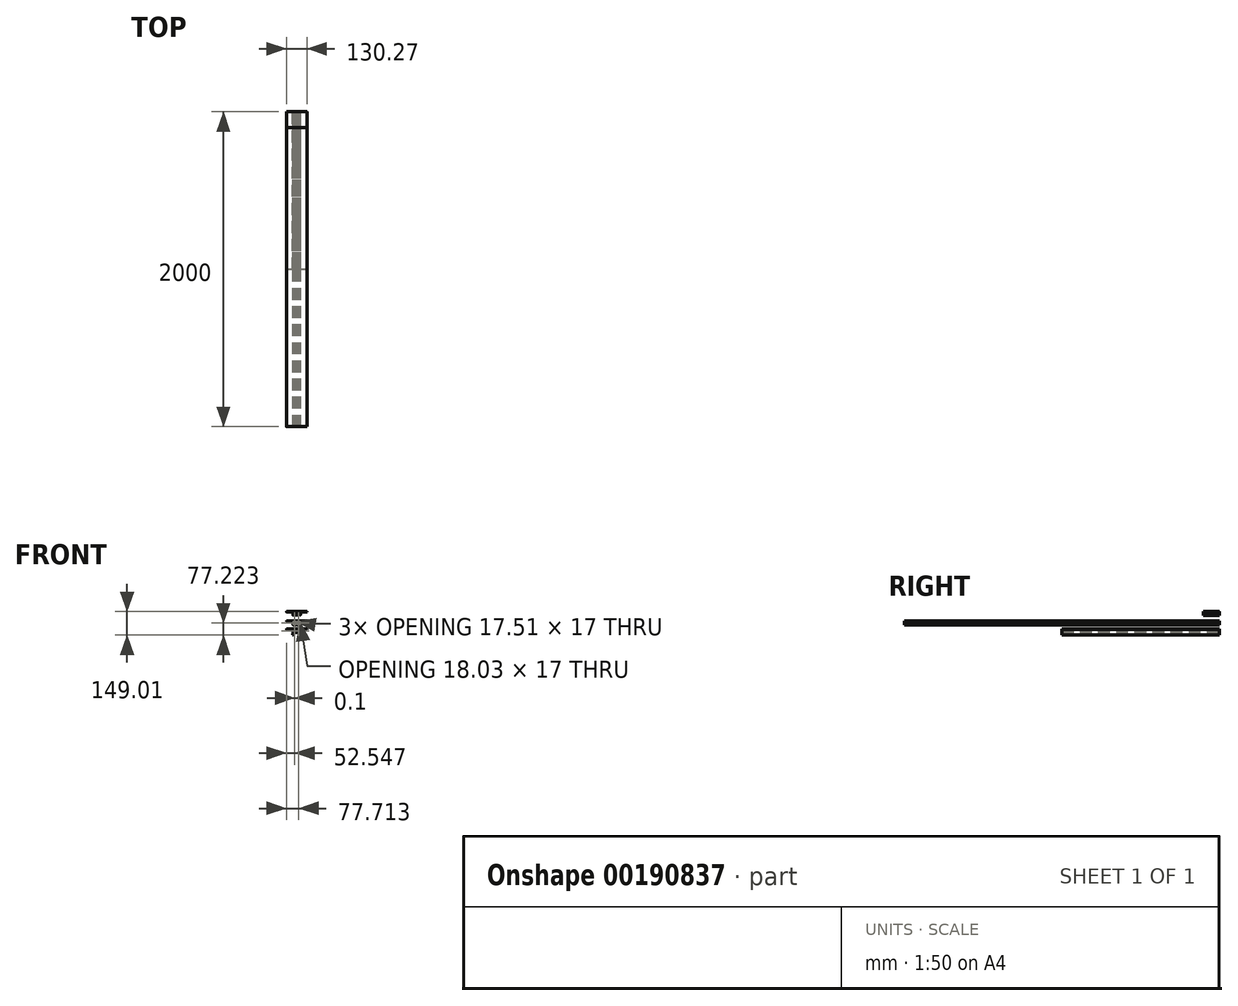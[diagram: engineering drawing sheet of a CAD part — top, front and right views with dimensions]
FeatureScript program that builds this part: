
annotation { "Feature Type Name" : "Feature", "Feature Type Description" : "" }
export const myFeature = defineFeature(function(context is Context, id is Id, definition is map)
    precondition{}
    {
        {
            var Q0;
            Q0=qCreatedBy(makeId("Front.planeOp"),FACE);
            var sketch = newSketch(context, id + "F0", { "sketchPlane" : qUnion([Q0])});
            skLineSegment(sketch, "E0", {"start": v(-63.5, 0) * mm, "end": v(63.5, 0) * mm});
            skLineSegment(sketch, "E1", {"start": v(-63.5, -3) * mm, "end": v(-25.2, -3) * mm});
            skLineSegment(sketch, "E2", {"start": v(24.22, -3) * mm, "end": v(63.5, -3) * mm});
            skLineSegment(sketch, "E3", {"start": v(-21.2, -7) * mm, "end": v(-21.2, -16) * mm});
            skLineSegment(sketch, "E4", {"start": v(-17.2, -20) * mm, "end": v(-10.5, -20) * mm});
            skLineSegment(sketch, "E5", {"start": v(-17.2, -3) * mm, "end": v(-5.7, -3) * mm});
            skArc(sketch, "E6", {"start": v(-4.66, -6.71) * mm, "mid": v(-8.45, -11.3) * mm, "end": v(-8.54, -17.26) * mm});
            skArc(sketch, "E7.filletArc", {"start": v(-4.66, -6.71) * mm, "mid": v(-3.77, -4.46) * mm, "end": v(-5.7, -3) * mm});
            skLineSegment(sketch, "E8", {"start": v(21.2, -7) * mm, "end": v(21.2, -7) * mm});
            skPoint(sketch, "E9.visualSharp", {"position": v(-21.2, -3) * mm});
            skArc(sketch, "E9.filletArc", {"start": v(-17.2, -3) * mm, "mid": v(-20.04, -4.17) * mm, "end": v(-21.2, -7) * mm});
            skPoint(sketch, "E10.visualSharp", {"position": v(-7.05, -20) * mm});
            skArc(sketch, "E10.filletArc", {"start": v(-10.5, -20) * mm, "mid": v(-8.82, -19.14) * mm, "end": v(-8.54, -17.26) * mm});
            skPoint(sketch, "E11.visualSharp", {"position": v(-21.2, -20) * mm});
            skArc(sketch, "E11.filletArc", {"start": v(-21.2, -16) * mm, "mid": v(-20.04, -18.83) * mm, "end": v(-17.2, -20) * mm});
            skPoint(sketch, "E12", {"position": v(-24.2, -23) * mm});
            skPoint(sketch, "E13", {"position": v(24.22, -23.12) * mm});
            skLineSegment(sketch, "E14", {"start": v(-24.2, -4) * mm, "end": v(-24.2, -22.88) * mm});
            skLineSegment(sketch, "E15", {"start": v(24.22, -3) * mm, "end": v(24.22, -23) * mm});
            skLineSegment(sketch, "E16.MirrorCS", {"start": v(25.48, -38) * mm, "end": v(25.48, -38) * mm});
            skArc(sketch, "E17", {"start": v(-63.5, 0) * mm, "mid": v(-65, -1.5) * mm, "end": v(-63.5, -3) * mm});
            skArc(sketch, "E18", {"start": v(63.5, -3) * mm, "mid": v(65, -1.5) * mm, "end": v(63.5, 0) * mm});
            skLineSegment(sketch, "E19", {"start": v(-24.22, -23.12) * mm, "end": v(-26.05, -38) * mm});
            skLineSegment(sketch, "E20", {"start": v(-24.3, -36.44) * mm, "end": v(-21.78, -24.58) * mm});
            skLineSegment(sketch, "E21", {"start": v(-19.82, -23) * mm, "end": v(-2.72, -23) * mm});
            skLineSegment(sketch, "E22", {"start": v(-1.72, -22) * mm, "end": v(-1.72, -20.86) * mm});
            skPoint(sketch, "E23.visualSharp", {"position": v(-21.44, -23) * mm});
            skArc(sketch, "E23.filletArc", {"start": v(-19.82, -23) * mm, "mid": v(-21.08, -23.45) * mm, "end": v(-21.78, -24.58) * mm});
            skPoint(sketch, "E24.visualSharp", {"position": v(-24.63, -38) * mm});
            skArc(sketch, "E24.filletArc", {"start": v(-26.05, -38) * mm, "mid": v(-24.92, -37.5) * mm, "end": v(-24.3, -36.44) * mm});
            skArc(sketch, "E25.filletArc", {"start": v(-24.22, -23.12) * mm, "mid": v(-24.21, -23) * mm, "end": v(-24.2, -22.88) * mm});
            skPoint(sketch, "E26.visualSharp", {"position": v(-24.2, -3) * mm});
            skArc(sketch, "E26.filletArc", {"start": v(-24.2, -4) * mm, "mid": v(-24.5, -3.3) * mm, "end": v(-25.2, -3) * mm});
            skPoint(sketch, "E27.visualSharp", {"position": v(-1.72, -23) * mm});
            skArc(sketch, "E28.filletArc", {"start": v(-1.72, -20.86) * mm, "mid": v(-1.89, -20.3) * mm, "end": v(-2.33, -19.94) * mm});
            skArc(sketch, "E29.MirrorCS", {"start": v(1.72, -20.86) * mm, "mid": v(1.89, -20.3) * mm, "end": v(2.33, -19.94) * mm});
            skLineSegment(sketch, "E30.MirrorCS", {"start": v(1.72, -22) * mm, "end": v(1.72, -20.86) * mm});
            skLineSegment(sketch, "E31.MirrorCS", {"start": v(19.82, -23) * mm, "end": v(2.72, -23) * mm});
            skArc(sketch, "E32.MirrorCS", {"start": v(19.82, -23) * mm, "mid": v(21.08, -23.45) * mm, "end": v(21.78, -24.58) * mm});
            skLineSegment(sketch, "E33.MirrorCS", {"start": v(24.3, -36.44) * mm, "end": v(21.78, -24.58) * mm});
            skLineSegment(sketch, "E34.MirrorCS", {"start": v(24.24, -23.24) * mm, "end": v(26.05, -38) * mm});
            skArc(sketch, "E35.MirrorCS", {"start": v(26.05, -38) * mm, "mid": v(24.92, -37.5) * mm, "end": v(24.3, -36.44) * mm});
            skArc(sketch, "E36", {"start": v(-2.33, -19.94) * mm, "mid": v(0, -8.41) * mm, "end": v(2.33, -19.94) * mm});
            skArc(sketch, "E37.filletArc", {"start": v(24.22, -23) * mm, "mid": v(24.23, -23.12) * mm, "end": v(24.24, -23.24) * mm});
            skArc(sketch, "E38.MirrorCS", {"start": v(4.66, -6.71) * mm, "mid": v(8.45, -11.3) * mm, "end": v(8.54, -17.26) * mm});
            skArc(sketch, "E39.MirrorCS", {"start": v(4.66, -6.71) * mm, "mid": v(3.77, -4.46) * mm, "end": v(5.7, -3) * mm});
            skArc(sketch, "E40.MirrorCS", {"start": v(17.2, -3) * mm, "mid": v(20.04, -4.17) * mm, "end": v(21.2, -7) * mm});
            skLineSegment(sketch, "E41.MirrorCS", {"start": v(21.2, -7) * mm, "end": v(21.2, -16) * mm});
            skArc(sketch, "E42.MirrorCS", {"start": v(21.2, -16) * mm, "mid": v(20.04, -18.83) * mm, "end": v(17.2, -20) * mm});
            skLineSegment(sketch, "E43.MirrorCS", {"start": v(17.2, -20) * mm, "end": v(10.5, -20) * mm});
            skArc(sketch, "E44.MirrorCS", {"start": v(10.5, -20) * mm, "mid": v(8.82, -19.14) * mm, "end": v(8.54, -17.26) * mm});
            skLineSegment(sketch, "E45.MirrorCS", {"start": v(17.2, -3) * mm, "end": v(5.7, -3) * mm});
            skPoint(sketch, "E46.visualSharp", {"position": v(1.72, -23) * mm});
            skArc(sketch, "E46.filletArc", {"start": v(1.72, -22) * mm, "mid": v(2.02, -22.7) * mm, "end": v(2.72, -23) * mm});
            skArc(sketch, "E47.filletArc", {"start": v(-2.72, -23) * mm, "mid": v(-2.02, -22.7) * mm, "end": v(-1.72, -22) * mm});
            skLineSegment(sketch, "E48", {"start": v(-63.6, 50.71) * mm, "end": v(63.4, 50.71) * mm});
            skLineSegment(sketch, "E49", {"start": v(-63.6, 47.71) * mm, "end": v(-25.3, 47.71) * mm});
            skLineSegment(sketch, "E50", {"start": v(24.63, 47.71) * mm, "end": v(63.4, 47.71) * mm});
            skLineSegment(sketch, "E51", {"start": v(-21.3, 43.71) * mm, "end": v(-21.3, 34.71) * mm});
            skLineSegment(sketch, "E52", {"start": v(-17.3, 30.71) * mm, "end": v(-10.6, 30.71) * mm});
            skLineSegment(sketch, "E53", {"start": v(-17.3, 47.71) * mm, "end": v(-5.8, 47.71) * mm});
            skArc(sketch, "E54", {"start": v(-4.76, 44) * mm, "mid": v(-8.55, 39.4) * mm, "end": v(-8.64, 33.45) * mm});
            skArc(sketch, "E55.filletArc", {"start": v(-4.76, 44) * mm, "mid": v(-3.87, 46.25) * mm, "end": v(-5.8, 47.71) * mm});
            skLineSegment(sketch, "E56", {"start": v(21.63, 43.71) * mm, "end": v(21.63, 43.72) * mm});
            skPoint(sketch, "E57.visualSharp", {"position": v(-21.3, 47.71) * mm});
            skArc(sketch, "E57.filletArc", {"start": v(-17.3, 47.71) * mm, "mid": v(-20.14, 46.54) * mm, "end": v(-21.3, 43.71) * mm});
            skPoint(sketch, "E58.visualSharp", {"position": v(-7.15, 30.71) * mm});
            skArc(sketch, "E58.filletArc", {"start": v(-10.6, 30.71) * mm, "mid": v(-8.92, 31.58) * mm, "end": v(-8.64, 33.45) * mm});
            skPoint(sketch, "E59.visualSharp", {"position": v(-21.3, 30.71) * mm});
            skArc(sketch, "E59.filletArc", {"start": v(-21.3, 34.71) * mm, "mid": v(-20.14, 31.88) * mm, "end": v(-17.3, 30.71) * mm});
            skLineSegment(sketch, "E60", {"start": v(-24.3, 46.71) * mm, "end": v(-24.3, 28.71) * mm});
            skLineSegment(sketch, "E61", {"start": v(24.63, 47.71) * mm, "end": v(24.63, 28.71) * mm});
            skArc(sketch, "E62", {"start": v(-63.6, 50.71) * mm, "mid": v(-65.1, 49.21) * mm, "end": v(-63.6, 47.71) * mm});
            skArc(sketch, "E63", {"start": v(63.4, 47.71) * mm, "mid": v(64.9, 49.21) * mm, "end": v(63.4, 50.71) * mm});
            skLineSegment(sketch, "E64", {"start": v(-19.92, 27.71) * mm, "end": v(-2.82, 27.71) * mm});
            skLineSegment(sketch, "E65", {"start": v(-1.82, 28.71) * mm, "end": v(-1.82, 29.85) * mm});
            skPoint(sketch, "E66.visualSharp", {"position": v(-24.3, 47.71) * mm});
            skArc(sketch, "E66.filletArc", {"start": v(-24.3, 46.71) * mm, "mid": v(-24.6, 47.42) * mm, "end": v(-25.3, 47.71) * mm});
            skPoint(sketch, "E67.visualSharp", {"position": v(-1.82, 27.71) * mm});
            skArc(sketch, "E68.filletArc", {"start": v(-1.82, 29.85) * mm, "mid": v(-1.99, 30.4) * mm, "end": v(-2.43, 30.77) * mm});
            skArc(sketch, "E69.MirrorCS", {"start": v(1.62, 29.85) * mm, "mid": v(1.79, 30.4) * mm, "end": v(2.23, 30.77) * mm});
            skLineSegment(sketch, "E70.MirrorCS", {"start": v(1.62, 28.71) * mm, "end": v(1.62, 29.85) * mm});
            skLineSegment(sketch, "E71.MirrorCS", {"start": v(19.72, 27.71) * mm, "end": v(2.62, 27.71) * mm});
            skArc(sketch, "E72", {"start": v(-2.43, 30.77) * mm, "mid": v(-0.1, 42.3) * mm, "end": v(2.23, 30.77) * mm});
            skArc(sketch, "E73.MirrorCS", {"start": v(4.56, 44) * mm, "mid": v(8.35, 39.4) * mm, "end": v(8.44, 33.45) * mm});
            skArc(sketch, "E74.MirrorCS", {"start": v(4.56, 44) * mm, "mid": v(3.67, 46.25) * mm, "end": v(5.6, 47.71) * mm});
            skArc(sketch, "E75.MirrorCS", {"start": v(17.63, 47.71) * mm, "mid": v(20.46, 46.54) * mm, "end": v(21.63, 43.71) * mm});
            skLineSegment(sketch, "E76.MirrorCS", {"start": v(21.63, 43.71) * mm, "end": v(21.63, 34.71) * mm});
            skArc(sketch, "E77.MirrorCS", {"start": v(21.63, 34.71) * mm, "mid": v(20.46, 31.88) * mm, "end": v(17.63, 30.71) * mm});
            skLineSegment(sketch, "E78.MirrorCS", {"start": v(17.1, 30.71) * mm, "end": v(10.4, 30.71) * mm});
            skArc(sketch, "E79.MirrorCS", {"start": v(10.4, 30.71) * mm, "mid": v(8.72, 31.58) * mm, "end": v(8.44, 33.45) * mm});
            skLineSegment(sketch, "E80.MirrorCS", {"start": v(17.63, 47.71) * mm, "end": v(6.12, 47.71) * mm});
            skPoint(sketch, "E81.visualSharp", {"position": v(1.62, 27.71) * mm});
            skArc(sketch, "E81.filletArc", {"start": v(1.62, 28.71) * mm, "mid": v(1.92, 28) * mm, "end": v(2.62, 27.71) * mm});
            skArc(sketch, "E82.filletArc", {"start": v(-2.82, 27.71) * mm, "mid": v(-2.12, 28) * mm, "end": v(-1.82, 28.71) * mm});
            skLineSegment(sketch, "E83", {"start": v(-23.3, 27.71) * mm, "end": v(-19.92, 27.71) * mm});
            skLineSegment(sketch, "E84", {"start": v(23.63, 27.71) * mm, "end": v(19.72, 27.71) * mm});
            skPoint(sketch, "E85.visualSharp", {"position": v(-24.3, 27.71) * mm});
            skArc(sketch, "E85.filletArc", {"start": v(-24.3, 28.71) * mm, "mid": v(-24.02, 28) * mm, "end": v(-23.3, 27.71) * mm});
            skPoint(sketch, "E86.visualSharp", {"position": v(24.63, 27.71) * mm});
            skArc(sketch, "E86.filletArc", {"start": v(23.63, 27.71) * mm, "mid": v(24.34, 28) * mm, "end": v(24.63, 28.71) * mm});
            skLineSegment(sketch, "E87", {"start": v(6.12, 47.71) * mm, "end": v(5.6, 47.71) * mm});
            skLineSegment(sketch, "E88", {"start": v(17.63, 30.71) * mm, "end": v(17.1, 30.71) * mm});
            skLineSegment(sketch, "E89", {"start": v(-63.31, 111) * mm, "end": v(63.67, 111) * mm});
            skLineSegment(sketch, "E90", {"start": v(-63.31, 108) * mm, "end": v(-25.02, 108) * mm});
            skLineSegment(sketch, "E91", {"start": v(-21.02, 104) * mm, "end": v(-21.02, 89.43) * mm});
            skLineSegment(sketch, "E92", {"start": v(-17.02, 108) * mm, "end": v(-8.3, 108) * mm});
            skArc(sketch, "E93", {"start": v(-6.17, 102.88) * mm, "mid": v(-8.59, 94.45) * mm, "end": v(-2.7, 87.97) * mm});
            skArc(sketch, "E94.filletArc", {"start": v(-6.17, 102.88) * mm, "mid": v(-5.52, 106.15) * mm, "end": v(-8.3, 108) * mm});
            skPoint(sketch, "E95.visualSharp", {"position": v(-21.02, 108) * mm});
            skArc(sketch, "E95.filletArc", {"start": v(-17.02, 108) * mm, "mid": v(-19.85, 106.83) * mm, "end": v(-21.02, 104) * mm});
            skLineSegment(sketch, "E96", {"start": v(-24.02, 107) * mm, "end": v(-24.02, 89.43) * mm});
            skArc(sketch, "E97", {"start": v(-63.31, 111) * mm, "mid": v(-64.81, 109.5) * mm, "end": v(-63.31, 108) * mm});
            skArc(sketch, "E98", {"start": v(63.67, 108) * mm, "mid": v(65.17, 109.5) * mm, "end": v(63.67, 111) * mm});
            skLineSegment(sketch, "E99", {"start": v(-1.54, 88.92) * mm, "end": v(-1.54, 90.04) * mm});
            skPoint(sketch, "E100.visualSharp", {"position": v(-24.02, 108) * mm});
            skArc(sketch, "E100.filletArc", {"start": v(-24.02, 107) * mm, "mid": v(-24.31, 107.7) * mm, "end": v(-25.02, 108) * mm});
            skPoint(sketch, "E101.visualSharp", {"position": v(-1.54, 87.9) * mm});
            skArc(sketch, "E102.filletArc", {"start": v(-1.54, 90.04) * mm, "mid": v(-1.67, 90.54) * mm, "end": v(-2.03, 90.9) * mm});
            skArc(sketch, "E103.filletArc", {"start": v(-2.2, 87.97) * mm, "mid": v(-1.72, 88.34) * mm, "end": v(-1.54, 88.92) * mm});
            skLineSegment(sketch, "E104", {"start": v(0.18, 96.5) * mm, "end": v(0.18, 122.46) * mm, "construction": true});
            skLineSegment(sketch, "E105.MirrorCS", {"start": v(63.67, 108) * mm, "end": v(25.38, 108) * mm});
            skArc(sketch, "E106.MirrorCS", {"start": v(24.38, 107) * mm, "mid": v(24.67, 107.7) * mm, "end": v(25.38, 108) * mm});
            skLineSegment(sketch, "E107.MirrorCS", {"start": v(21.38, 104) * mm, "end": v(21.38, 89.43) * mm});
            skPoint(sketch, "E108.MirrorP", {"position": v(21.38, 108) * mm});
            skPoint(sketch, "E109.MirrorP", {"position": v(24.38, 108) * mm});
            skLineSegment(sketch, "E110.MirrorCS", {"start": v(24.38, 107) * mm, "end": v(24.38, 89.43) * mm});
            skArc(sketch, "E111.MirrorCS", {"start": v(17.38, 108) * mm, "mid": v(20.2, 106.83) * mm, "end": v(21.38, 104) * mm});
            skLineSegment(sketch, "E112.MirrorCS", {"start": v(17.38, 108) * mm, "end": v(8.65, 108) * mm});
            skArc(sketch, "E113.MirrorCS", {"start": v(6.53, 102.88) * mm, "mid": v(5.88, 106.15) * mm, "end": v(8.65, 108) * mm});
            skArc(sketch, "E114.MirrorCS", {"start": v(6.53, 102.88) * mm, "mid": v(8.94, 94.45) * mm, "end": v(3.05, 87.97) * mm});
            skArc(sketch, "E115.MirrorCS", {"start": v(2.57, 87.97) * mm, "mid": v(2.08, 88.34) * mm, "end": v(1.9, 88.92) * mm});
            skLineSegment(sketch, "E116.MirrorCS", {"start": v(1.9, 88.92) * mm, "end": v(1.9, 90.04) * mm});
            skPoint(sketch, "E117.MirrorP", {"position": v(1.9, 87.9) * mm});
            skArc(sketch, "E118.MirrorCS", {"start": v(1.9, 90.04) * mm, "mid": v(2.03, 90.54) * mm, "end": v(2.4, 90.9) * mm});
            skArc(sketch, "E119", {"start": v(2.4, 90.9) * mm, "mid": v(0.18, 102.48) * mm, "end": v(-2.03, 90.9) * mm});
            skLineSegment(sketch, "E120", {"start": v(24.38, 87.93) * mm, "end": v(-24.02, 87.93) * mm, "construction": true});
            skPoint(sketch, "E121.visualSharp", {"position": v(-2.53, 87.92) * mm});
            skArc(sketch, "E121.filletArc", {"start": v(-2.7, 87.97) * mm, "mid": v(-2.45, 87.93) * mm, "end": v(-2.2, 87.97) * mm});
            skPoint(sketch, "E122.visualSharp", {"position": v(2.89, 87.92) * mm});
            skArc(sketch, "E122.filletArc", {"start": v(2.57, 87.97) * mm, "mid": v(2.8, 87.93) * mm, "end": v(3.05, 87.97) * mm});
            skLineSegment(sketch, "E123", {"start": v(-22.52, 87.93) * mm, "end": v(-22.52, 87.93) * mm});
            skLineSegment(sketch, "E124", {"start": v(22.88, 87.93) * mm, "end": v(22.88, 87.93) * mm});
            skPoint(sketch, "E125.visualSharp", {"position": v(-24.02, 87.93) * mm});
            skArc(sketch, "E125.filletArc", {"start": v(-24.02, 89.43) * mm, "mid": v(-23.58, 88.37) * mm, "end": v(-22.52, 87.93) * mm});
            skPoint(sketch, "E126.visualSharp", {"position": v(-21.02, 87.93) * mm});
            skArc(sketch, "E126.filletArc", {"start": v(-22.52, 87.93) * mm, "mid": v(-21.46, 88.37) * mm, "end": v(-21.02, 89.43) * mm});
            skPoint(sketch, "E127.visualSharp", {"position": v(21.38, 87.93) * mm});
            skArc(sketch, "E127.filletArc", {"start": v(21.38, 89.43) * mm, "mid": v(21.82, 88.37) * mm, "end": v(22.88, 87.93) * mm});
            skPoint(sketch, "E128.visualSharp", {"position": v(24.38, 87.93) * mm});
            skArc(sketch, "E128.filletArc", {"start": v(22.88, 87.93) * mm, "mid": v(23.94, 88.37) * mm, "end": v(24.38, 89.43) * mm});
            skSolve(sketch);
        }
        {
            var Q0;
            Q0=makeQuery(id+"F0.imprint","IMPRINT",FACE,{"disambiguationData":[TD([[makeQuery(id+"F0.imprint","IMPRINT",EDGE,{"derivedFrom":sQuery(id+"F0.wireOp",EDGE,"E0")}),-1.0]])]});
            extrude(context, id + "F1", {"entities" : qUnion([Q0]), "depth" : 1000 * mm, "offsetDistance" : 25 * mm});
        }
        {
            var Q0;
            Q0=makeQuery(id+"F0.imprint","IMPRINT",FACE,{"disambiguationData":[TD([[makeQuery(id+"F0.imprint","IMPRINT",EDGE,{"derivedFrom":sQuery(id+"F0.wireOp",EDGE,"E48")}),-1.0]])]});
            extrude(context, id + "F2", {"entities" : qUnion([Q0]), "depth" : 2000 * mm, "offsetDistance" : 25 * mm});
        }
        {
            var Q0;
            Q0=makeQuery(id+"F0.imprint","IMPRINT",FACE,{"disambiguationData":[TD([[makeQuery(id+"F0.imprint","IMPRINT",EDGE,{"derivedFrom":sQuery(id+"F0.wireOp",EDGE,"E89")}),-1.0]])]});
            extrude(context, id + "F3", {"entities" : qUnion([Q0]), "depth" : 100 * mm, "offsetDistance" : 25 * mm});
        }
    });
